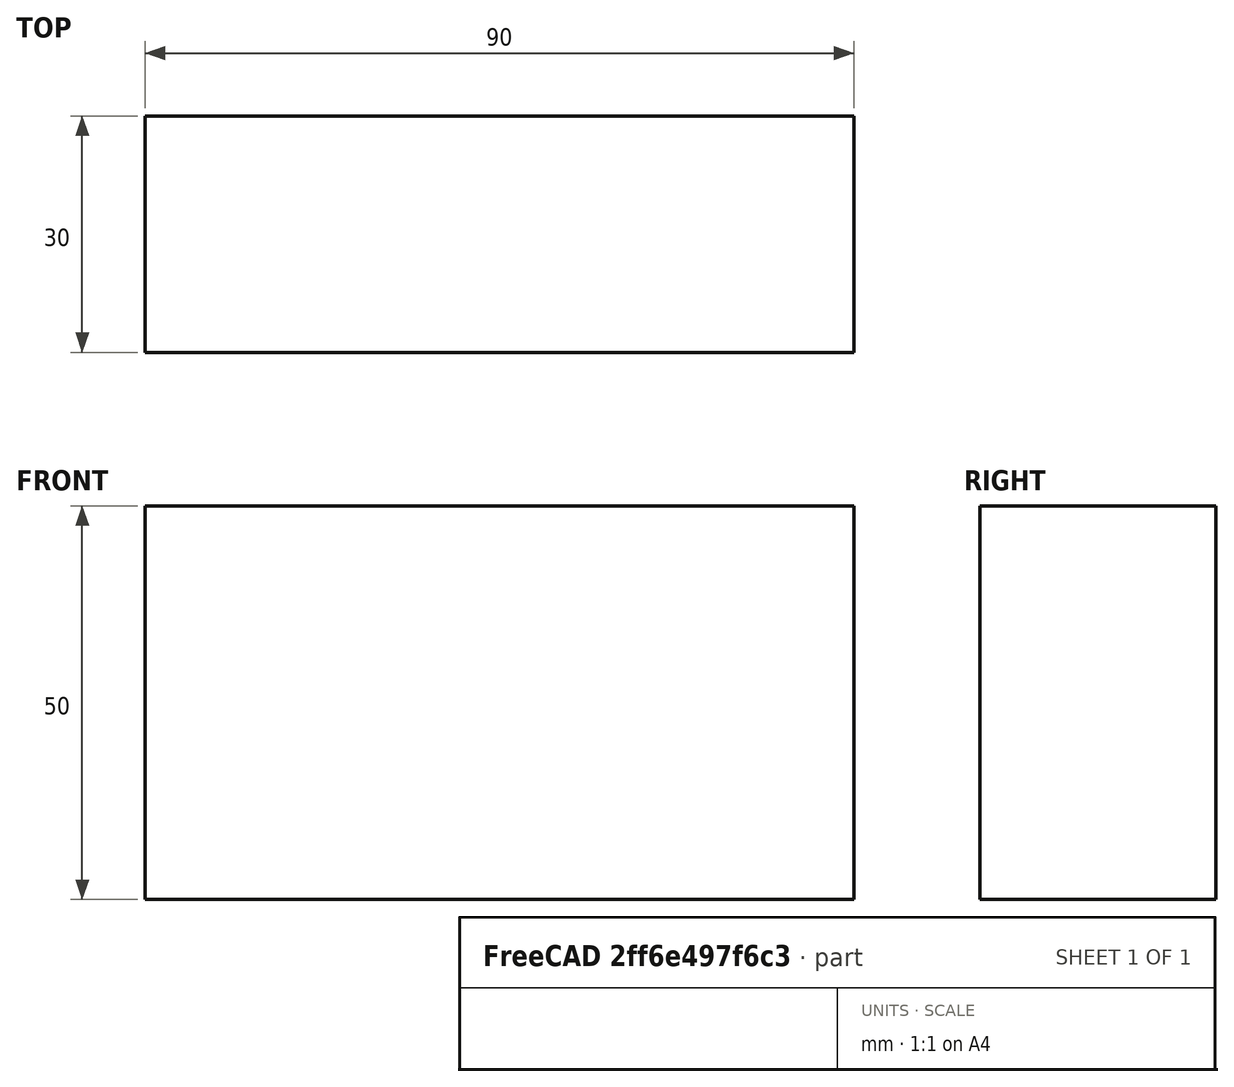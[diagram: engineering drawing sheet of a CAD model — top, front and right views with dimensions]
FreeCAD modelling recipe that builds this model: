
FCSTD DOCUMENT  (FreeCAD 0.15R4671 (Git))
Label: Flat Bar 90x30 EN10058 S235JR
License: All rights reserved
LicenseURL: http://en.wikipedia.org/wiki/All_rights_reserved
objects: Sketcher::SketchObject×1, Part::Extrusion×1
note: 2 computed .brp shape members not serialized (recipe doc carries the construction recipe); baked Part::Feature solids carry a one-line shape summary decoded from their .brp

FEATURE [Sketcher::SketchObject] Sketch
  sketch-geometry (4):
    g0: LineSegment StartX=-45 StartY=-15 StartZ=0 EndX=45 EndY=-15 EndZ=0
    g1: LineSegment StartX=45 StartY=-15 StartZ=0 EndX=45 EndY=15 EndZ=0
    g2: LineSegment StartX=45 StartY=15 StartZ=0 EndX=-45 EndY=15 EndZ=0
    g3: LineSegment StartX=-45 StartY=15 StartZ=0 EndX=-45 EndY=-15 EndZ=0
  constraints (12):
    c: Coincident(g0,g1)
    c: Coincident(g1,g2)
    c: Coincident(g2,g3)
    c: Coincident(g3,g0)
    c: Horizontal(g0)
    c: Horizontal(g2)
    c: Vertical(g1)
    c: Vertical(g3)
    c: Symmetric(g1,g2,g-2)
    c: Symmetric(g0,g1,g-1)
    c: DistanceY(g1) = 30
    c: DistanceX(g0) = 90
FEATURE [Part::Extrusion] Extrude  label="Flat Bar 90x30 EN10058 S235JR"
  Base = -> Sketch
  Dir = (0,0,50)
  Solid = true
